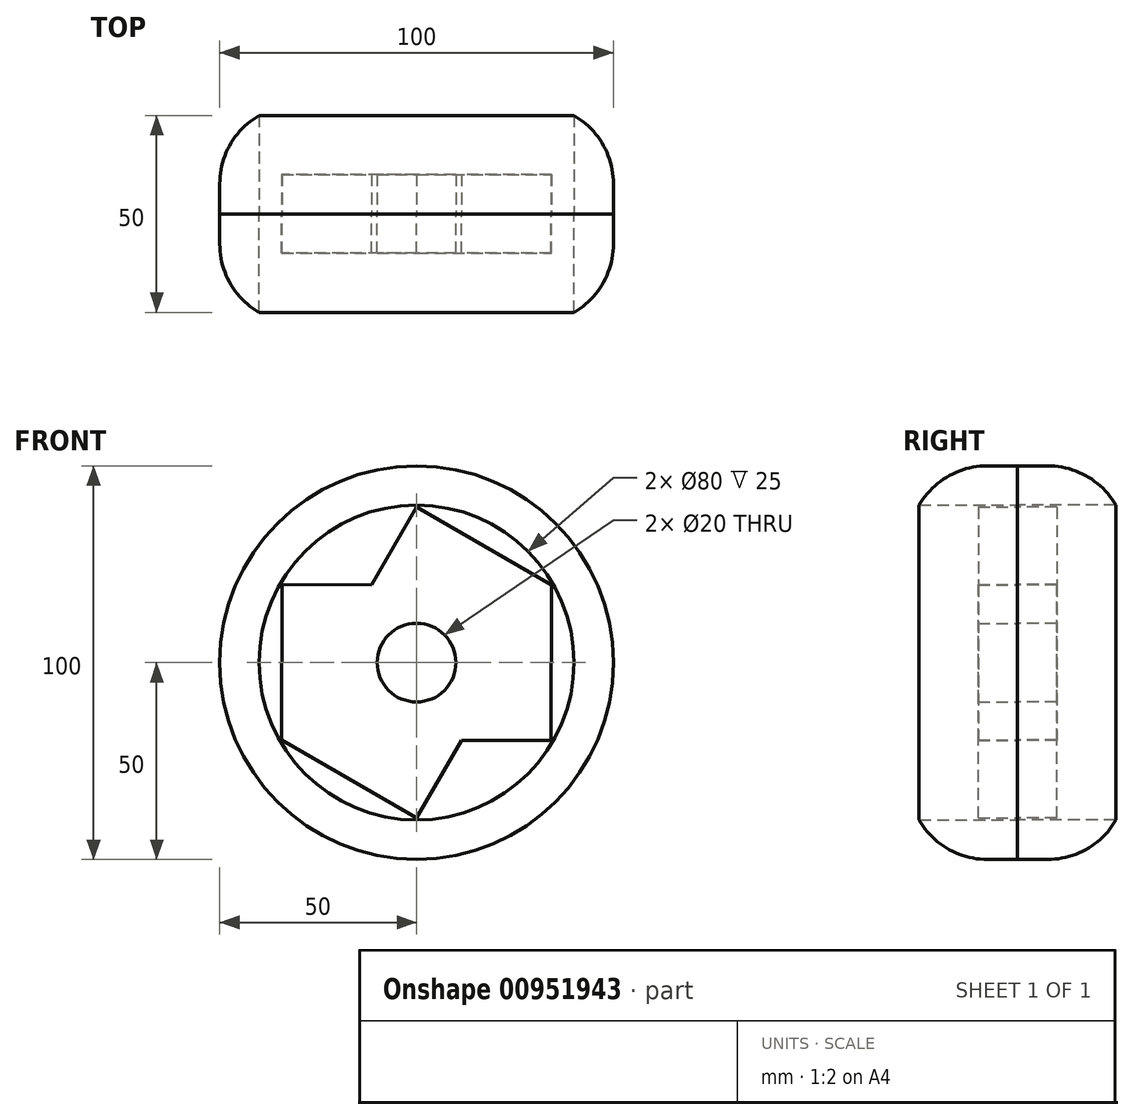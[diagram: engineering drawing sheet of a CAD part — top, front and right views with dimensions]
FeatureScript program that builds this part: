
annotation { "Feature Type Name" : "Feature", "Feature Type Description" : "" }
export const myFeature = defineFeature(function(context is Context, id is Id, definition is map)
    precondition{}
    {
        {
            var Q0;
            Q0=qCreatedBy(makeId("Front.planeOp"),FACE);
            var sketch = newSketch(context, id + "F0", { "sketchPlane" : qUnion([Q0])});
            skCircle(sketch, "E0", {"center": v(0, 0) * mm, "radius": 50 * mm});
            skCircle(sketch, "E1", {"center": v(0, 0) * mm, "radius": 40 * mm});
            skCircle(sketch, "E2.cCircle", {"center": v(0, 0) * mm, "radius": 34.2 * mm, "construction": true});
            skLineSegment(sketch, "E2.0", {"start": v(0.05, 39.5) * mm, "end": v(34.23, 19.7) * mm});
            skLineSegment(sketch, "E2.1", {"start": v(34.23, 19.7) * mm, "end": v(34.18, -19.79) * mm});
            skLineSegment(sketch, "E2.2", {"start": v(34.18, -19.79) * mm, "end": v(-0.05, -39.5) * mm});
            skLineSegment(sketch, "E2.3", {"start": v(-0.05, -39.5) * mm, "end": v(-34.23, -19.7) * mm});
            skLineSegment(sketch, "E2.4", {"start": v(-34.23, -19.7) * mm, "end": v(-34.18, 19.79) * mm});
            skLineSegment(sketch, "E2.5", {"start": v(-34.18, 19.79) * mm, "end": v(0.05, 39.5) * mm});
            skPoint(sketch, "E2.0.midPoint", {"position": v(17.14, 29.6) * mm});
            skCircle(sketch, "E3", {"center": v(0, 0) * mm, "radius": 10 * mm});
            skLineSegment(sketch, "E4", {"start": v(-34.18, 19.79) * mm, "end": v(-11.38, 19.76) * mm});
            skLineSegment(sketch, "E5", {"start": v(0.05, 39.5) * mm, "end": v(-11.38, 19.76) * mm});
            skLineSegment(sketch, "E6", {"start": v(34.18, -19.79) * mm, "end": v(11.38, -19.76) * mm});
            skLineSegment(sketch, "E7", {"start": v(-0.05, -39.5) * mm, "end": v(11.38, -19.76) * mm});
            skPoint(sketch, "E8.orphan", {"position": v(-22.82, 0) * mm});
            skPoint(sketch, "E9.orphan", {"position": v(0, 19.75) * mm});
            skPoint(sketch, "E10.orphan", {"position": v(22.82, 0) * mm});
            skPoint(sketch, "E11.orphan", {"position": v(0, -19.75) * mm});
            skSolve(sketch);
        }
        {
            var Q0;
            Q0=makeQuery(id+"F0.imprint","IMPRINT",FACE,{"disambiguationData":[TD([[makeQuery(id+"F0.imprint","IMPRINT",EDGE,{"derivedFrom":sQuery(id+"F0.wireOp",EDGE,"E2.0")}),-1.0]])]});
            extrude(context, id + "F1", {"entities" : qUnion([Q0]), "depth" : 10 * mm, "offsetDistance" : 25 * mm});
        }
        {
            var Q0;
            Q0=makeQuery(id+"F0.imprint","IMPRINT",FACE,{"disambiguationData":[TD([[makeQuery(id+"F0.imprint","IMPRINT",EDGE,{"derivedFrom":sQuery(id+"F0.wireOp",EDGE,"E0")}),1.0]])]});
            extrude(context, id + "F2", {"entities" : qUnion([Q0]), "depth" : 25 * mm, "offsetDistance" : 25 * mm});
        }
        {
            var Q0;
            Q0=makeQuery(id+"F2.opExtrude","SWEPT_BODY",BODY,{"disambiguationData":[OSD([sQuery(id+"F0.wireOp",EDGE,"E0"),sQuery(id+"F0.wireOp",EDGE,"E1")])]});
            var Q1;
            Q1=makeQuery(id+"F1.opExtrude","SWEPT_BODY",BODY,{"disambiguationData":[OSD([sQuery(id+"F0.wireOp",EDGE,"E2.0"),sQuery(id+"F0.wireOp",EDGE,"E2.1"),sQuery(id+"F0.wireOp",EDGE,"E2.2"),sQuery(id+"F0.wireOp",EDGE,"E2.3"),sQuery(id+"F0.wireOp",EDGE,"E2.4"),sQuery(id+"F0.wireOp",EDGE,"E2.5"),sQuery(id+"F0.wireOp",EDGE,"E3")])]});
            var Q2;
            Q2=qCreatedBy(makeId("Front.planeOp"),FACE);
            mirror(context, id + "F3", {"entities" : qUnion([Q0, Q1]), "mirrorPlane" : qUnion([Q2])});
        }
        {
            var Q0;
            Q0=makeQuery(id+"F2.opExtrude","CAP_EDGE",EDGE,{"disambiguationData":[OSD([sQuery(id+"F0.wireOp",EDGE,"E0")])],"isStart":false});
            var Q1;
            Q1=makeQuery(id+"F3.opPattern","COPY",EDGE,{"derivedFrom":makeQuery(id+"F2.opExtrude","CAP_EDGE",EDGE,{"disambiguationData":[OSD([sQuery(id+"F0.wireOp",EDGE,"E0")])],"isStart":false}),"instanceName":"1"});
            fillet(context, id + "F4", {"entities" : qUnion([Q0, Q1]), "radius" : 20 * mm, "tangentPropagation" : true, "allowEdgeOverflow" : false});
        }
    });
